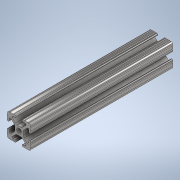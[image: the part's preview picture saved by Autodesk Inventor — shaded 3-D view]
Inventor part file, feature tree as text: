
AUTODESK INVENTOR PART (.ipt)
format: ipt  version: 2020 (Build 240168000, 168)  size: 239,104 bytes
history: native  units: in
note: dims shown in document units (in); Inventor stores cm internally (conversion verified against a paired STEP export)
features: extrude x1, sketch x1
ambient origin geometry x8: Origin, YZ Plane, XZ Plane, XY Plane, X Axis, Y Axis, Z Axis, Center Point
bodies: Solid1 (feature_tree)
feature tree (2):
  extrude  "Extrusion1"  [1 undecoded]
  sketch  "Sketch1"  dims[d0=6.0in d1=0.0in]
note: 1 required parameter value undecoded (feature->parameter linkage not recoverable at this tier; creation-order binding heuristic only, values carry confidence <= 0.55)
